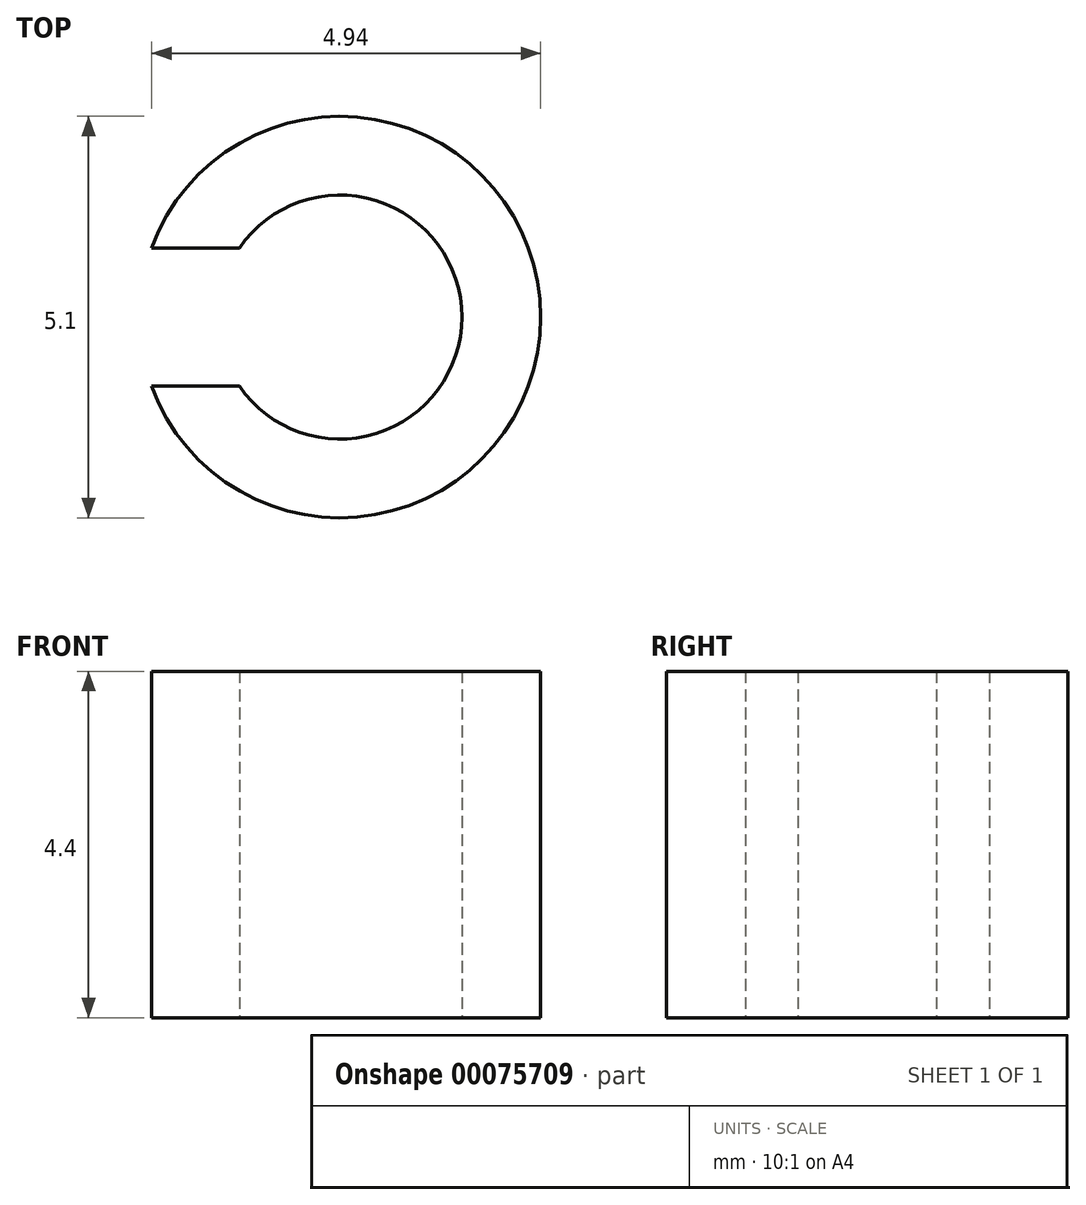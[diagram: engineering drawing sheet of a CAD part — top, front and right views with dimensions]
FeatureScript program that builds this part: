
annotation { "Feature Type Name" : "Feature", "Feature Type Description" : "" }
export const myFeature = defineFeature(function(context is Context, id is Id, definition is map)
    precondition{}
    {
        {
            var Q0;
            Q0=qCreatedBy(makeId("Top.planeOp"),FACE);
            var sketch = newSketch(context, id + "F0", { "sketchPlane" : qUnion([Q0])});
            skCircle(sketch, "E0", {"center": v(0, 0) * mm, "radius": 2.55 * mm});
            skCircle(sketch, "E1", {"center": v(0, 0) * mm, "radius": 1.55 * mm});
            skLineSegment(sketch, "E2.bottom", {"start": v(-3.9, -0.88) * mm, "end": v(3.9, -0.88) * mm});
            skLineSegment(sketch, "E2.top", {"start": v(-3.9, 0.88) * mm, "end": v(3.9, 0.88) * mm});
            skLineSegment(sketch, "E2.left", {"start": v(-3.9, -0.88) * mm, "end": v(-3.9, 0.88) * mm});
            skLineSegment(sketch, "E2.right", {"start": v(3.9, -0.88) * mm, "end": v(3.9, 0.88) * mm});
            skPoint(sketch, "E3.start.orphan", {"position": v(0, -1.55) * mm});
            skSolve(sketch);
        }
        {
            var Q0;
            {var subQ0=sQuery(id+"F0.wireOp",EDGE,"E2.bottom");var subQ1=sQuery(id+"F0.wireOp",EDGE,"E0");var subQ2=makeQuery(id+"F0.imprint","INTERSECT",VERTEX,{"disambiguationData":[OD(0.0)],"derivedFrom":[subQ1,subQ0]});Q0=makeQuery(id+"F0.imprint","IMPRINT",FACE,{"disambiguationData":[TD([[makeQuery(id+"F0.imprint","IMPRINT",EDGE,{"disambiguationData":[TD([[subQ2,-1.0]])],"derivedFrom":subQ1}),1.0]])]});}
            var Q1;
            {var subQ0=sQuery(id+"F0.wireOp",EDGE,"E2.top");var subQ1=sQuery(id+"F0.wireOp",EDGE,"E0");var subQ2=makeQuery(id+"F0.imprint","INTERSECT",VERTEX,{"disambiguationData":[OD(1.0)],"derivedFrom":[subQ1,subQ0]});Q1=makeQuery(id+"F0.imprint","IMPRINT",FACE,{"disambiguationData":[TD([[makeQuery(id+"F0.imprint","IMPRINT",EDGE,{"disambiguationData":[TD([[subQ2,1.0]])],"derivedFrom":subQ1}),1.0]])]});}
            var Q2;
            {var subQ0=sQuery(id+"F0.wireOp",EDGE,"E2.top");var subQ1=sQuery(id+"F0.wireOp",EDGE,"E0");var subQ2=makeQuery(id+"F0.imprint","INTERSECT",VERTEX,{"disambiguationData":[OD(0.0)],"derivedFrom":[subQ1,subQ0]});Q2=makeQuery(id+"F0.imprint","IMPRINT",FACE,{"disambiguationData":[TD([[makeQuery(id+"F0.imprint","IMPRINT",EDGE,{"disambiguationData":[TD([[subQ2,1.0]])],"derivedFrom":subQ1}),1.0]])]});}
            extrude(context, id + "F1", {"entities" : qUnion([Q0, Q1, Q2]), "endBound" : BoundingType.SYMMETRIC, "depth" : 4.4 * mm});
        }
    });
